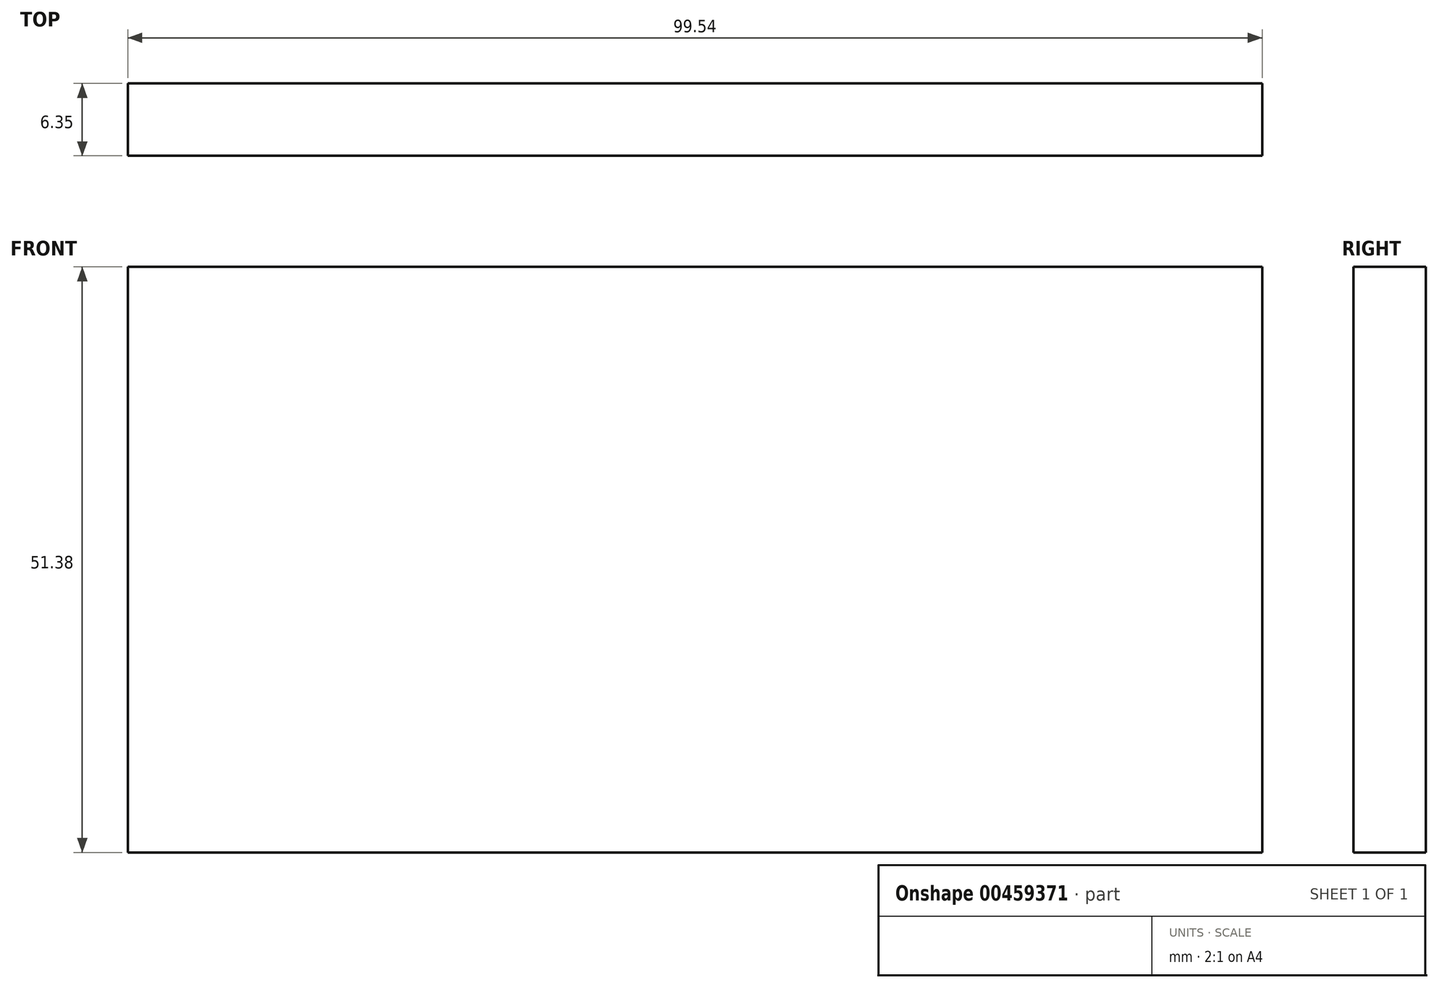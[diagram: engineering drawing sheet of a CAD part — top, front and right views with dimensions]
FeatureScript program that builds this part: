
annotation { "Feature Type Name" : "Feature", "Feature Type Description" : "" }
export const myFeature = defineFeature(function(context is Context, id is Id, definition is map)
    precondition{}
    {
        {
            var Q0;
            Q0=qCreatedBy(makeId("Front.planeOp"),FACE);
            var sketch = newSketch(context, id + "F0", { "sketchPlane" : qUnion([Q0])});
            skLineSegment(sketch, "E0.bottom", {"start": v(-64.65, 0) * mm, "end": v(34.89, 0) * mm});
            skLineSegment(sketch, "E0.top", {"start": v(-64.65, 51.38) * mm, "end": v(34.89, 51.38) * mm});
            skLineSegment(sketch, "E0.left", {"start": v(-64.65, 0) * mm, "end": v(-64.65, 51.38) * mm});
            skLineSegment(sketch, "E0.right", {"start": v(34.89, 0) * mm, "end": v(34.89, 51.38) * mm});
            skSolve(sketch);
        }
        {
            var Q0;
            Q0=makeQuery(id+"F0.imprint","IMPRINT",FACE,{"disambiguationData":[TD([[makeQuery(id+"F0.imprint","IMPRINT",EDGE,{"derivedFrom":sQuery(id+"F0.wireOp",EDGE,"E0.bottom")}),1.0]])]});
            extrude(context, id + "F1", {"entities" : qUnion([Q0]), "depth" : 6.35 * mm});
        }
    });
